# Revit family: Drain-Green_Roof-Jay R. Smith-Round_Type-1937_Series
name_source: partatom
category: Plumbing Fixtures
units: mm (PartAtom-declared; Revit-internal decimal feet)

## family parameters
Always vertical = Yes
Cut with Voids When Loaded = No
OmniClass Number = 23.70.50.21.24.11
OmniClass Title = Roof Waste Water Drains
Part Type = Normal
Room Calculation Point = No
Round Connector Dimension = Use Radius
Shared = No
Work Plane-Based = Yes

## types (21) — shared parameters
304SS - All Type 304 Stainless Steel = No
316SS - All Type 316 Stainless Steel = No
AD - Aluminum Dome = No
AE - Adjustable Extension = No
Assembly Code = D2040200
Body Material = Cast Iron-Jay R Smith-Duco Coated
CID - Cast Iron Dome = No
CIDG - Galvanized Cast Iron Dome = No
CW Connection = No
Default Elevation = 0"
Description = Green Roof Planter Drain
Dome Cover Material = Metal-Jay R Smith-Stainless Steel
Dome Material = PVC-Jay R Smith-White
E - Extension (specify height) = No
G - Galvanized Cast Iron Body & Collar = No
HW Connection = No
Installation Type = Roof Mounted
L - Speedi-Set Service Weight - 02"(50), 03"(75) & 04"(100) sizes only = No
LXH - Speedi-Set Extra Heavy - 02"(50), 03"(75) & 04"(100) sizes only = No
Manufacturer = Jay R. Smith
Material = Cast Iron-Jay R Smith-Duco Coated
Perforated Gravel Stop Height = 6"
Product Documentation Link = https://www.jrsmith.com
Product Page URL = https://www.jrsmith.com
RBD - Rough Bronze Dome = No
RDP - Roof Deck Plate = No
SP2, -SP3 or -SP4 - Internal Waterdam Standpipe = No
SSM - Standpipe Covered with Stainless Steel Mesh = No
U - Vandal Proof = No
URL = http://www.jrsmith.com
Vent Connection = No
Waste Connection = Yes

## per-type parameters (varying)
| type | Bottom Depth B | Connection Description | D - Overall Diameter | E Diameter | Outlet Diameter | Outlet Radius |
| 1937Y02 | 5" | 2" No-HUB Outlet Connection | 15 1/4" | 11" | 2" | 1" |
| 1937Y03 | 5" | 3" No-HUB Outlet Connection | 15 1/4" | 11" | 3" | 1 1/2" |
| 1937Y04 | 5" | 4" No-HUB Outlet Connection | 15 1/4" | 11" | 4" | 2" |
| 1937Y05 | 5" | 5" No-HUB Outlet Connection | 15 1/4" | 11" | 5" | 2 1/2" |
| 1937Y06 | 5" | 6" No-HUB Outlet Connection | 15 1/4" | 11" | 6" | 3" |
| 1937Y08 | 7 3/4" | 8" No-HUB Outlet Connection | 20" | 16" | 8" | 4" |
| 1937Y10 | 7 3/4" | 10" No-HUB Outlet Connection | 20" | 16" | 10" | 5" |
| 1937C02 | 5" | 2" Caulk Outlet Connection | 15 1/4" | 11" | 2" | 1" |
| 1937C03 | 5" | 3" Caulk Outlet Connection | 15 1/4" | 11" | 3" | 1 1/2" |
| 1937C04 | 5" | 4" Caulk Outlet Connection | 15 1/4" | 11" | 4" | 2" |
| 1937C05 | 5" | 5" Caulk Outlet Connection | 15 1/4" | 11" | 5" | 2 1/2" |
| 1937C06 | 5" | 6" Caulk Outlet Connection | 15 1/4" | 11" | 6" | 3" |
| 1937C08 | 7 3/4" | 8" Caulk Outlet Connection | 20" | 16" | 8" | 4" |
| 1937C10 | 7 3/4" | 10" Caulk Outlet Connection | 20" | 16" | 10" | 5" |
| 1937T02 | 3 3/4" | 2" Threaded Outlet Connection | 15 1/4" | 11" | 2" | 1" |
| 1937T03 | 3 3/4" | 3" Threaded Outlet Connection | 15 1/4" | 11" | 3" | 1 1/2" |
| 1937T04 | 3 3/4" | 4" Threaded Outlet Connection | 15 1/4" | 11" | 4" | 2" |
| 1937T05 | 3 3/4" | 5" Threaded Outlet Connection | 15 1/4" | 11" | 5" | 2 1/2" |
| 1937T06 | 3 3/4" | 6" Threaded Outlet Connection | 15 1/4" | 11" | 6" | 3" |
| 1937T08 | 7 3/4" | 8" Threaded Outlet Connection | 20" | 16" | 8" | 4" |
| 1937T10 | 7 3/4" | 10" Threaded Outlet Connection | 20" | 16" | 10" | 5" |

note: column(s) folded — value = type name in every type: Model

## geometry (parser evidence)
native form markers: Sweep x4
no freeform markers — native parametric forms only
